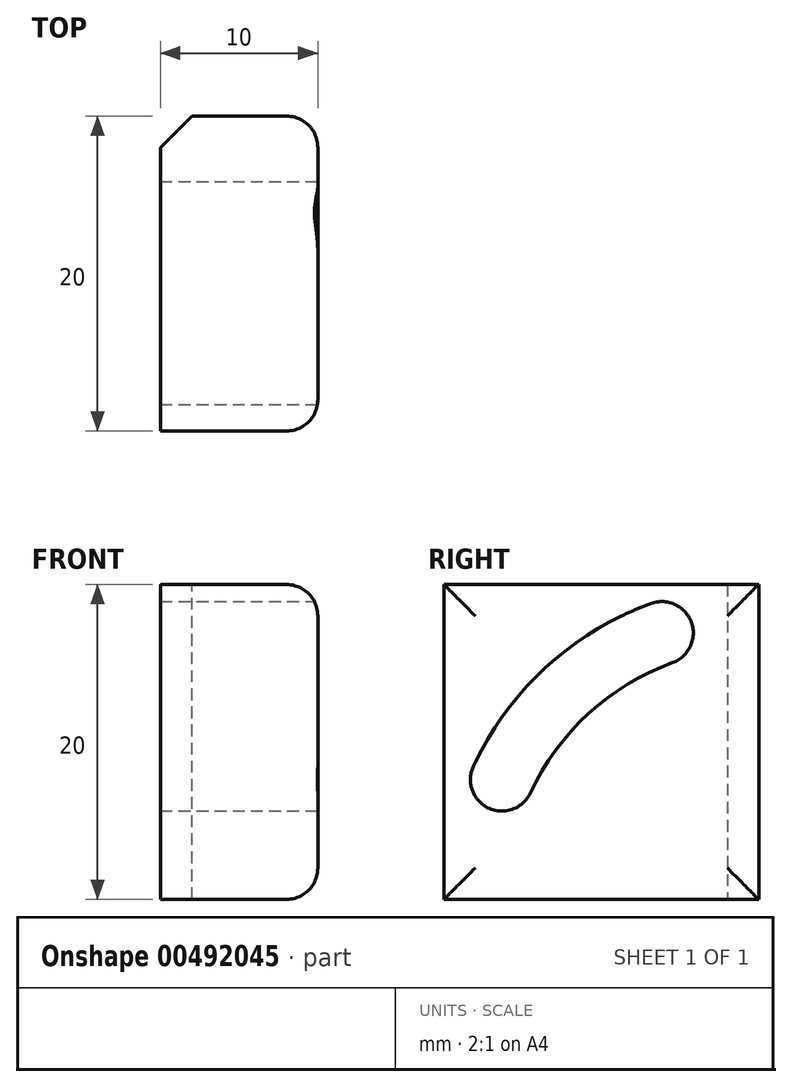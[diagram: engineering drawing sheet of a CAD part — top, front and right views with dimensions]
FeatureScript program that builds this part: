
annotation { "Feature Type Name" : "Feature", "Feature Type Description" : "" }
export const myFeature = defineFeature(function(context is Context, id is Id, definition is map)
    precondition{}
    {
        {
            var Q0;
            Q0=qCreatedBy(makeId("Front.planeOp"),FACE);
            var sketch = newSketch(context, id + "F0", { "sketchPlane" : qUnion([Q0])});
            skLineSegment(sketch, "E0.bottom", {"start": v(0, 20) * mm, "end": v(10, 20) * mm});
            skLineSegment(sketch, "E0.top", {"start": v(0, 0) * mm, "end": v(10, 0) * mm});
            skLineSegment(sketch, "E0.left", {"start": v(0, 20) * mm, "end": v(0, 0) * mm});
            skLineSegment(sketch, "E0.right", {"start": v(10, 20) * mm, "end": v(10, 0) * mm});
            skSolve(sketch);
        }
        {
            var Q0;
            Q0 = qSketchRegion(id + "F0", true);
            extrude(context, id + "F1", {"entities" : qUnion([Q0]), "depth" : 20 * mm});
        }
        {
            var Q0;
            Q0=makeQuery(id+"F1.opExtrude","SWEPT_FACE",FACE,{"disambiguationData":[OSD([sQuery(id+"F0.wireOp",EDGE,"E0.right")])]});
            fillet(context, id + "F2", {"entities" : qUnion([Q0]), "radius" : 2 * mm, "tangentPropagation" : true, "allowEdgeOverflow" : false});
        }
        {
            var Q0;
            Q0=makeQuery(id+"F1.opExtrude","CAP_EDGE",EDGE,{"disambiguationData":[OSD([sQuery(id+"F0.wireOp",EDGE,"E0.left")])],"isStart":true});
            chamfer(context, id + "F3", {"entities" : qUnion([Q0]), "width" : 2 * mm, "tangentPropagation" : true});
        }
        {
            var Q0;
            Q0=makeQuery(id+"F1.opExtrude","SWEPT_FACE",FACE,{"disambiguationData":[OSD([sQuery(id+"F0.wireOp",EDGE,"E0.right")])]});
            var sketch = newSketch(context, id + "F4", { "sketchPlane" : qUnion([Q0])});
            skCircle(sketch, "E1", {"center": v(0, 0) * mm, "radius": 18 * mm, "construction": true});
            skArc(sketch, "E2", {"start": v(-6.84, 18.8) * mm, "mid": v(-13.51, 14.75) * mm, "end": v(-18.13, 8.45) * mm});
            skArc(sketch, "E3", {"start": v(-5.47, 15.04) * mm, "mid": v(-10.8, 11.8) * mm, "end": v(-14.5, 6.76) * mm});
            skLineSegment(sketch, "E4", {"start": v(0, 0) * mm, "end": v(-6.16, 16.91) * mm, "construction": true});
            skLineSegment(sketch, "E5", {"start": v(0, 0) * mm, "end": v(-16.31, 7.6) * mm, "construction": true});
            skArc(sketch, "E6", {"start": v(-5.47, 15.04) * mm, "mid": v(-4.28, 17.6) * mm, "end": v(-6.84, 18.8) * mm});
            skArc(sketch, "E7", {"start": v(-18.13, 8.45) * mm, "mid": v(-17.16, 5.8) * mm, "end": v(-14.5, 6.76) * mm});
            skSolve(sketch);
        }
        {
            var Q0;
            Q0 = qSketchRegion(id + "F4", true);
            extrude(context, id + "F5", {"entities" : qUnion([Q0]), "operationType" : NewBodyOperationType.REMOVE, "oppositeDirection" : true, "depth" : 24.4 * mm, "offsetDistance" : 25 * mm});
        }
    });
